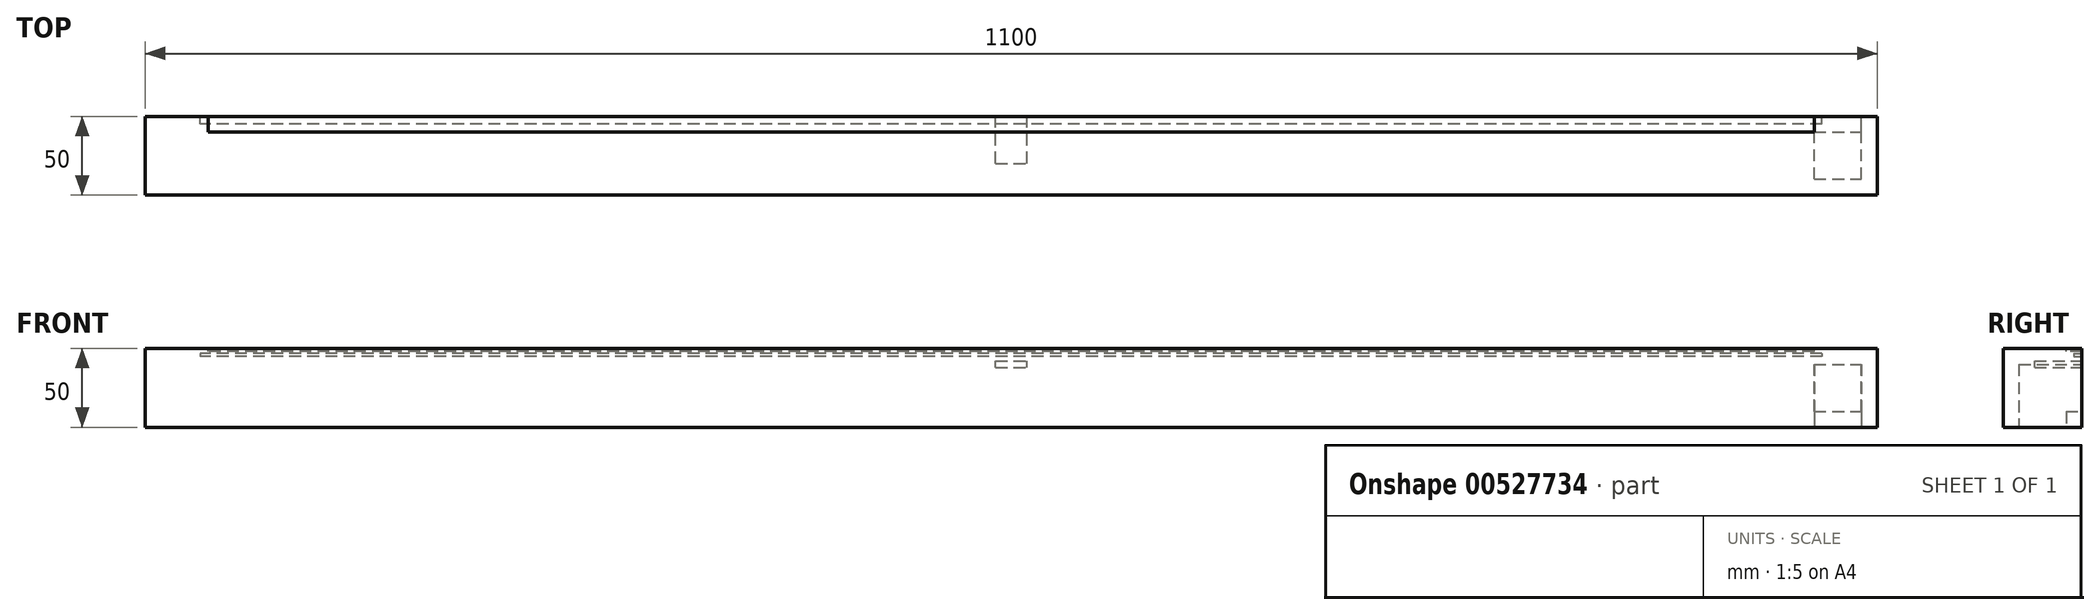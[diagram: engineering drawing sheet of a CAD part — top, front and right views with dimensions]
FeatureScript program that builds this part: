
annotation { "Feature Type Name" : "Feature", "Feature Type Description" : "" }
export const myFeature = defineFeature(function(context is Context, id is Id, definition is map)
    precondition{}
    {
        {
            var Q0;
            Q0=qCreatedBy(makeId("Top.planeOp"),FACE);
            var sketch = newSketch(context, id + "F0", { "sketchPlane" : qUnion([Q0])});
            skLineSegment(sketch, "E0.bottom", {"start": v(0, 0) * mm, "end": v(-1100, 0) * mm});
            skLineSegment(sketch, "E0.top", {"start": v(0, -50) * mm, "end": v(-1100, -50) * mm});
            skLineSegment(sketch, "E0.left", {"start": v(0, 0) * mm, "end": v(0, -50) * mm});
            skLineSegment(sketch, "E0.right", {"start": v(-1100, 0) * mm, "end": v(-1100, -50) * mm});
            skSolve(sketch);
        }
        {
            var Q0;
            Q0=makeQuery(id+"F0.imprint","IMPRINT",FACE,{"disambiguationData":[TD([[makeQuery(id+"F0.imprint","IMPRINT",EDGE,{"derivedFrom":sQuery(id+"F0.wireOp",EDGE,"E0.bottom")}),1.0]])]});
            extrude(context, id + "F1", {"entities" : qUnion([Q0]), "depth" : 50 * mm, "offsetDistance" : 25 * mm});
        }
        {
            var Q0;
            Q0=makeQuery(id+"F1.opExtrude","CAP_FACE",FACE,{"disambiguationData":[OSD([sQuery(id+"F0.wireOp",EDGE,"E0.bottom"),sQuery(id+"F0.wireOp",EDGE,"E0.top"),sQuery(id+"F0.wireOp",EDGE,"E0.left"),sQuery(id+"F0.wireOp",EDGE,"E0.right")])],"isStart":true});
            var sketch = newSketch(context, id + "F2", { "sketchPlane" : qUnion([Q0])});
            skLineSegment(sketch, "E1.bottom", {"start": v(-40, 40) * mm, "end": v(-10, 40) * mm});
            skLineSegment(sketch, "E1.top", {"start": v(-40, 10) * mm, "end": v(-10, 10) * mm});
            skLineSegment(sketch, "E1.left", {"start": v(-40, 40) * mm, "end": v(-40, 10) * mm});
            skLineSegment(sketch, "E1.right", {"start": v(-10, 40) * mm, "end": v(-10, 10) * mm});
            skSolve(sketch);
        }
        {
            var Q0;
            Q0 = qSketchRegion(id + "F2", true);
            extrude(context, id + "F3", {"entities" : qUnion([Q0]), "operationType" : NewBodyOperationType.REMOVE, "oppositeDirection" : true, "depth" : 40 * mm, "offsetDistance" : 25 * mm});
        }
        {
            var Q0;
            Q0=makeQuery(id+"F1.opExtrude","SWEPT_FACE",FACE,{"disambiguationData":[OSD([sQuery(id+"F0.wireOp",EDGE,"E0.right")])]});
            cPlane(context, id + "F4", {"entities" : qUnion([Q0]), "cplaneType" : CPlaneType.OFFSET, "offset" : 550 * mm, "oppositeDirection" : true, "width" : 150 * mm, "height" : 150 * mm});
        }
        {
            var Q0;
            Q0=makeQuery(id+"F1.opExtrude","CAP_FACE",FACE,{"disambiguationData":[OSD([sQuery(id+"F0.wireOp",EDGE,"E0.bottom"),sQuery(id+"F0.wireOp",EDGE,"E0.top"),sQuery(id+"F0.wireOp",EDGE,"E0.left"),sQuery(id+"F0.wireOp",EDGE,"E0.right")])],"isStart":false});
            var sketch = newSketch(context, id + "F5", { "sketchPlane" : qUnion([Q0])});
            skLineSegment(sketch, "E2.bottom", {"start": v(-40, 0) * mm, "end": v(-1060, 0) * mm});
            skLineSegment(sketch, "E2.top", {"start": v(-40, -10) * mm, "end": v(-1060, -10) * mm});
            skLineSegment(sketch, "E2.left", {"start": v(-40, 0) * mm, "end": v(-40, -10) * mm});
            skLineSegment(sketch, "E2.right", {"start": v(-1060, 0) * mm, "end": v(-1060, -10) * mm});
            skSolve(sketch);
        }
        {
            var Q0;
            Q0=makeQuery(id+"F5.imprint","IMPRINT",FACE,{"disambiguationData":[TD([[makeQuery(id+"F5.imprint","IMPRINT",EDGE,{"derivedFrom":sQuery(id+"F5.wireOp",EDGE,"E2.bottom")}),1.0]])]});
            extrude(context, id + "F6", {"entities" : qUnion([Q0]), "operationType" : NewBodyOperationType.REMOVE, "oppositeDirection" : true, "depth" : 2 * mm, "offsetDistance" : 25 * mm});
        }
        {
            var Q0;
            Q0=makeQuery(id+"F1.opExtrude","SWEPT_FACE",FACE,{"disambiguationData":[OSD([sQuery(id+"F0.wireOp",EDGE,"E0.bottom")])]});
            var sketch = newSketch(context, id + "F7", { "sketchPlane" : qUnion([Q0])});
            skLineSegment(sketch, "E3.bottom", {"start": v(35, 47) * mm, "end": v(1065, 47) * mm});
            skLineSegment(sketch, "E3.top", {"start": v(35, 45) * mm, "end": v(1065, 45) * mm});
            skLineSegment(sketch, "E3.left", {"start": v(35, 47) * mm, "end": v(35, 45) * mm});
            skLineSegment(sketch, "E3.right", {"start": v(1065, 47) * mm, "end": v(1065, 45) * mm});
            skSolve(sketch);
        }
        {
            var Q0;
            Q0 = qSketchRegion(id + "F7", true);
            extrude(context, id + "F8", {"entities" : qUnion([Q0]), "operationType" : NewBodyOperationType.REMOVE, "oppositeDirection" : true, "depth" : 5 * mm, "offsetDistance" : 25 * mm});
        }
        {
            var Q0;
            Q0=makeQuery(id+"F1.opExtrude","SWEPT_FACE",FACE,{"disambiguationData":[OSD([sQuery(id+"F0.wireOp",EDGE,"E0.bottom")])]});
            var sketch = newSketch(context, id + "F9", { "sketchPlane" : qUnion([Q0])});
            skLineSegment(sketch, "E4.bottom", {"start": v(40, 10) * mm, "end": v(10, 10) * mm});
            skLineSegment(sketch, "E4.top", {"start": v(40, 40) * mm, "end": v(10, 40) * mm});
            skLineSegment(sketch, "E4.left", {"start": v(40, 10) * mm, "end": v(40, 40) * mm});
            skLineSegment(sketch, "E4.right", {"start": v(10, 10) * mm, "end": v(10, 40) * mm});
            skPoint(sketch, "E4.middle", {"position": v(25, 25) * mm});
            skSolve(sketch);
        }
        {
            var Q0;
            Q0 = qSketchRegion(id + "F9", true);
            extrude(context, id + "F10", {"entities" : qUnion([Q0]), "operationType" : NewBodyOperationType.REMOVE, "oppositeDirection" : true, "depth" : 40 * mm, "offsetDistance" : 25 * mm});
        }
        {
            var Q0;
            Q0=makeQuery(id+"F1.opExtrude","SWEPT_FACE",FACE,{"disambiguationData":[OSD([sQuery(id+"F0.wireOp",EDGE,"E0.bottom")])]});
            var sketch = newSketch(context, id + "F11", { "sketchPlane" : qUnion([Q0])});
            skLineSegment(sketch, "E5.bottom", {"start": v(560, 38) * mm, "end": v(540, 38) * mm});
            skLineSegment(sketch, "E5.top", {"start": v(560, 42) * mm, "end": v(540, 42) * mm});
            skLineSegment(sketch, "E5.left", {"start": v(560, 38) * mm, "end": v(560, 42) * mm});
            skLineSegment(sketch, "E5.right", {"start": v(540, 38) * mm, "end": v(540, 42) * mm});
            skPoint(sketch, "E5.middle", {"position": v(550, 40) * mm});
            skSolve(sketch);
        }
        {
            var Q0;
            Q0 = qSketchRegion(id + "F11", true);
            extrude(context, id + "F12", {"entities" : qUnion([Q0]), "operationType" : NewBodyOperationType.REMOVE, "oppositeDirection" : true, "depth" : 30 * mm, "offsetDistance" : 25 * mm});
        }
    });
